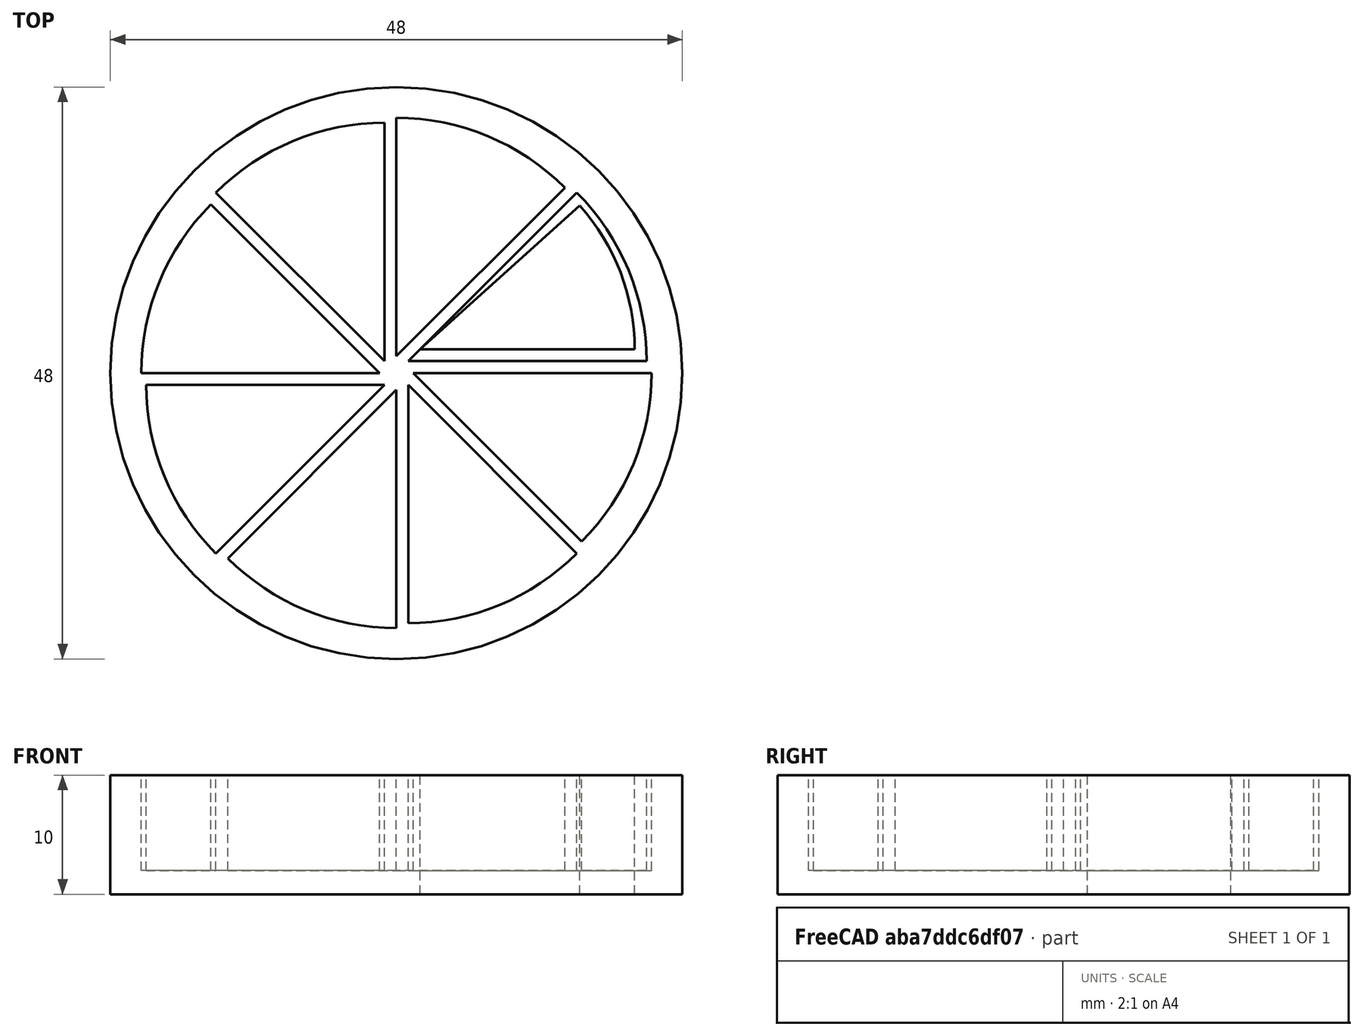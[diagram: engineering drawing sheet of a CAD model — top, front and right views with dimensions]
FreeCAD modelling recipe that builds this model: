
FCSTD DOCUMENT  (FreeCAD 0.20R29177 +426 (Git))
Label: Queso
License: All rights reserved
LicenseURL: http://en.wikipedia.org/wiki/All_rights_reserved
objects: Part::Cylinder×3, Part::FeaturePython×1, Part::Cut×1
note: 4 computed .brp shape members not serialized (recipe doc carries the construction recipe); baked Part::Feature solids carry a one-line shape summary decoded from their .brp

FEATURE [Part::Cylinder] Cylinder  label="Cilindro"
  Angle = 360
  AttacherType = Attacher::AttachEngine3D
  FirstAngle = 0
  Height = 10
  Radius = 24
  SecondAngle = 0
FEATURE [Part::Cylinder] Cylinder001  label="Cilindro001"
  Angle = 45
  AttacherType = Attacher::AttachEngine3D
  FirstAngle = 0
  Height = 8
  Placement = pos=(1,1,2) rot=(0,0,1;0rad)
  Radius = 20
  SecondAngle = 0
FEATURE [Part::FeaturePython] Array  # Draft array (typed FeaturePython)
  AlwaysSyncPlacement = false
  Angle = 360
  ArrayType = 1
  Axis = (0,0,1)
  Base = -> Cylinder001
  Center = (0,0,0)
  Count = 8
  ExpandArray = false
  Fuse = false
  IntervalAxis = (0,0,0)
  IntervalX = (50,0,0)
  IntervalY = (0,50,0)
  IntervalZ = (0,0,50)
  NumberCircles = 3
  NumberPolar = 8
  NumberX = 2
  NumberY = 2
  NumberZ = 1
  PlacementList = 8 placements: [(1,1,2),(0,1.41421,2),(-1,1,2),(-1.41421,2.22045e-16,2),(-1,-1,2),(0,-1.41421,2),(1,-1,2),(1.41421,-2.22045e-16,2)]
  RadialDistance = 50
  ScaleList = (8) [(1,1,1),(1,1,1),(1,1,1),(1,1,1),(1,1,1),(1,1,1),(1,1,1),(1,1,1)]
  Symmetry = 1
  TangentialDistance = 25
FEATURE [Part::Cut] Cut
  Base = -> Cylinder
  Refine = true
  Tool = -> Array
FEATURE [Part::Cylinder] Cylinder002  label="Cilindro002"
  Angle = 42
  AttacherType = Attacher::AttachEngine3D
  FirstAngle = 0
  Height = 10
  Placement = pos=(2,2,0) rot=(0,0,1;0rad)
  Radius = 18
  SecondAngle = 0
